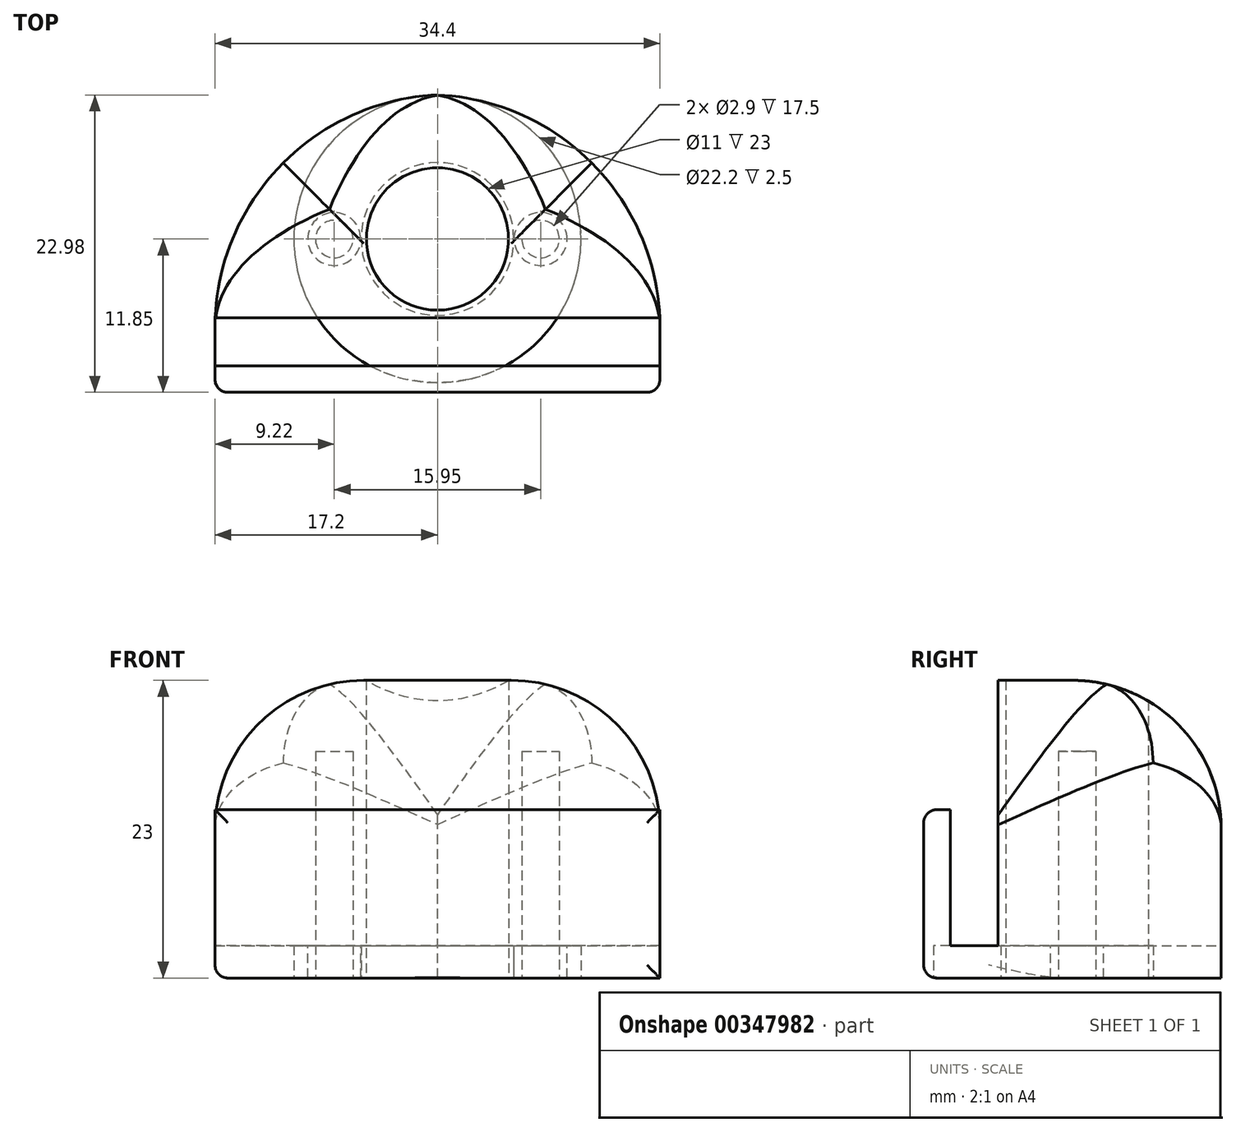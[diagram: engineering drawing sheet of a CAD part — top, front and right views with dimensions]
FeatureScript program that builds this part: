
annotation { "Feature Type Name" : "Feature", "Feature Type Description" : "" }
export const myFeature = defineFeature(function(context is Context, id is Id, definition is map)
    precondition{}
    {
        {
            var Q0;
            Q0=qCreatedBy(makeId("Top.planeOp"),FACE);
            var sketch = newSketch(context, id + "F0", { "sketchPlane" : qUnion([Q0])});
            skCircle(sketch, "E0", {"center": v(0, 0) * mm, "radius": 5.5 * mm});
            skLineSegment(sketch, "E1.bottom", {"start": v(17.2, 11.15) * mm, "end": v(-17.2, 11.15) * mm});
            skLineSegment(sketch, "E1.top", {"start": v(17.2, -11.85) * mm, "end": v(-17.2, -11.85) * mm});
            skLineSegment(sketch, "E1.left", {"start": v(17.2, 11.15) * mm, "end": v(17.2, -11.85) * mm});
            skLineSegment(sketch, "E1.right", {"start": v(-17.2, 11.15) * mm, "end": v(-17.2, -11.85) * mm});
            skPoint(sketch, "E1.middle", {"position": v(0, -0.35) * mm});
            skSolve(sketch);
        }
        {
            var Q0;
            Q0=makeQuery(id+"F0.imprint","IMPRINT",FACE,{"disambiguationData":[TD([[makeQuery(id+"F0.imprint","IMPRINT",EDGE,{"derivedFrom":sQuery(id+"F0.wireOp",EDGE,"E0")}),-1.0]])]});
            extrude(context, id + "F1", {"entities" : qUnion([Q0]), "depth" : 23 * mm});
        }
        {
            var Q0;
            Q0=makeQuery(id+"F1.opExtrude","CAP_FACE",FACE,{"disambiguationData":[OSD([sQuery(id+"F0.wireOp",EDGE,"E0"),sQuery(id+"F0.wireOp",EDGE,"E1.bottom"),sQuery(id+"F0.wireOp",EDGE,"E1.top"),sQuery(id+"F0.wireOp",EDGE,"E1.left"),sQuery(id+"F0.wireOp",EDGE,"E1.right"),sQuery(id+"F0.wireOp",EDGE,"J5Xj3zVj-uTtx-Os8S-LOdU-LLNhaVreQnM7")])],"isStart":true});
            var sketch = newSketch(context, id + "F2", { "sketchPlane" : qUnion([Q0])});
            skCircle(sketch, "E2", {"center": v(0, 0) * mm, "radius": 11.1 * mm});
            skCircle(sketch, "E3", {"center": v(0, 0) * mm, "radius": 5.3 * mm});
            skCircle(sketch, "E4", {"center": v(0, 0) * mm, "radius": 5.9 * mm});
            skSolve(sketch);
        }
        {
            var Q0;
            Q0=makeQuery(id+"F2.imprint","IMPRINT",FACE,{"disambiguationData":[TD([[makeQuery(id+"F2.imprint","IMPRINT",EDGE,{"derivedFrom":sQuery(id+"F2.wireOp",EDGE,"E2")}),1.0]])]});
            extrude(context, id + "F3", {"entities" : qUnion([Q0]), "operationType" : NewBodyOperationType.REMOVE, "oppositeDirection" : true, "depth" : 2.5 * mm});
        }
        {
            var Q0;
            Q0=makeQuery(id+"F3.boolean.opBoolean","COPY",FACE,{"derivedFrom":makeQuery(id+"F3.opExtrude","CAP_FACE",FACE,{"disambiguationData":[OSD([sQuery(id+"F0.wireOp",EDGE,"E0"),sQuery(id+"F2.wireOp",EDGE,"E2")])],"isStart":false})});
            var sketch = newSketch(context, id + "F4", { "sketchPlane" : qUnion([Q0])});
            skCircle(sketch, "E5", {"center": v(-7.98, 0) * mm, "radius": 1.45 * mm});
            skCircle(sketch, "E6", {"center": v(7.97, 0) * mm, "radius": 1.45 * mm});
            skCircle(sketch, "E7", {"center": v(7.97, 0) * mm, "radius": 2.05 * mm});
            skCircle(sketch, "E8", {"center": v(-7.98, 0) * mm, "radius": 2.05 * mm});
            skSolve(sketch);
        }
        {
            var Q0;
            Q0=makeQuery(id+"F4.imprint","IMPRINT",FACE,{"disambiguationData":[TD([[makeQuery(id+"F4.imprint","IMPRINT",EDGE,{"derivedFrom":sQuery(id+"F4.wireOp",EDGE,"E6")}),1.0]])]});
            var Q1;
            Q1=makeQuery(id+"F4.imprint","IMPRINT",FACE,{"disambiguationData":[TD([[makeQuery(id+"F4.imprint","IMPRINT",EDGE,{"derivedFrom":sQuery(id+"F4.wireOp",EDGE,"E5")}),1.0]])]});
            extrude(context, id + "F5", {"entities" : qUnion([Q0, Q1]), "operationType" : NewBodyOperationType.REMOVE, "oppositeDirection" : true, "depth" : 15 * mm});
        }
        {
            var Q0;
            Q0=makeQuery(id+"F1.opExtrude","CAP_FACE",FACE,{"disambiguationData":[OSD([sQuery(id+"F0.wireOp",EDGE,"E0"),sQuery(id+"F0.wireOp",EDGE,"E1.bottom"),sQuery(id+"F0.wireOp",EDGE,"E1.top"),sQuery(id+"F0.wireOp",EDGE,"E1.left"),sQuery(id+"F0.wireOp",EDGE,"E1.right"),sQuery(id+"F0.wireOp",EDGE,"J5Xj3zVj-uTtx-Os8S-LOdU-LLNhaVreQnM7")])],"isStart":false});
            var sketch = newSketch(context, id + "F6", { "sketchPlane" : qUnion([Q0])});
            skLineSegment(sketch, "E9", {"start": v(-17.2, -6.1) * mm, "end": v(17.2, -6.1) * mm});
            skLineSegment(sketch, "E10", {"start": v(17.2, -6.1) * mm, "end": v(17.2, -9.8) * mm});
            skLineSegment(sketch, "E11", {"start": v(17.2, -9.8) * mm, "end": v(-17.2, -9.8) * mm});
            skSolve(sketch);
        }
        {
            var Q0;
            {var subQ0=sQuery(id+"F6.wireOp",EDGE,"E9");Q0=makeQuery(id+"F6.imprint","IMPRINT",FACE,{"disambiguationData":[TD([[makeQuery(id+"F6.imprint","IMPRINT",EDGE,{"derivedFrom":subQ0}),-1.0]])]});}
            extrude(context, id + "F7", {"entities" : qUnion([Q0]), "operationType" : NewBodyOperationType.REMOVE, "oppositeDirection" : true, "depth" : 20.5 * mm});
        }
        {
            var Q0;
            {var subQ0=sQuery(id+"F6.wireOp",EDGE,"E11");Q0=makeQuery(id+"F6.imprint","IMPRINT",FACE,{"disambiguationData":[TD([[makeQuery(id+"F6.imprint","IMPRINT",EDGE,{"derivedFrom":subQ0}),1.0]])]});}
            extrude(context, id + "F8", {"entities" : qUnion([Q0]), "operationType" : NewBodyOperationType.REMOVE, "oppositeDirection" : true, "depth" : 10 * mm});
        }
        {
            var Q0;
            {var subQ0=sQuery(id+"F0.wireOp",EDGE,"E1.right");var subQ1=sQuery(id+"F0.wireOp",EDGE,"E1.bottom");Q0=makeQuery(id+"F7.boolean.opBoolean","SPLIT",EDGE,{"disambiguationData":[TD([makeQuery(id+"F1.opExtrude","SWEPT_FACE",FACE,{"disambiguationData":[OSD([subQ1])]})])],"derivedFrom":makeQuery(id+"F1.opExtrude","CAP_EDGE",EDGE,{"disambiguationData":[OSD([subQ0])],"isStart":false})});}
            var Q1;
            Q1=makeQuery(id+"F1.opExtrude","CAP_EDGE",EDGE,{"disambiguationData":[OSD([sQuery(id+"F0.wireOp",EDGE,"E1.bottom")])],"isStart":false});
            var Q2;
            {var subQ0=sQuery(id+"F0.wireOp",EDGE,"E1.left");var subQ1=sQuery(id+"F0.wireOp",EDGE,"E1.bottom");Q2=makeQuery(id+"F7.boolean.opBoolean","SPLIT",EDGE,{"disambiguationData":[TD([makeQuery(id+"F1.opExtrude","SWEPT_FACE",FACE,{"disambiguationData":[OSD([subQ1])]})])],"derivedFrom":makeQuery(id+"F1.opExtrude","CAP_EDGE",EDGE,{"disambiguationData":[OSD([subQ0])],"isStart":false})});}
            var Q3;
            Q3=makeQuery(id+"F8.boolean.opBoolean","COPY",EDGE,{"derivedFrom":makeQuery(id+"F8.opExtrude","CAP_EDGE",EDGE,{"disambiguationData":[OSD([sQuery(id+"F0.wireOp",EDGE,"E1.right")])],"isStart":false})});
            var Q4;
            Q4=makeQuery(id+"F8.boolean.opBoolean","COPY",EDGE,{"derivedFrom":makeQuery(id+"F8.opExtrude","CAP_EDGE",EDGE,{"disambiguationData":[OSD([sQuery(id+"F0.wireOp",EDGE,"E1.left")])],"isStart":false})});
            fillet(context, id + "F9", {"entities" : qUnion([Q0, Q1, Q2, Q3, Q4]), "radius" : 11.5 * mm, "tangentPropagation" : true, "allowEdgeOverflow" : false});
        }
        {
            var Q0;
            Q0=makeQuery(id+"F7.boolean.opBoolean","COPY",EDGE,{"derivedFrom":makeQuery(id+"F7.opExtrude","CAP_EDGE",EDGE,{"disambiguationData":[OSD([sQuery(id+"F6.wireOp",EDGE,"E9")])],"isStart":true})});
            var Q1;
            Q1=makeQuery(id+"F8.boolean.opBoolean","COPY",EDGE,{"derivedFrom":makeQuery(id+"F8.opExtrude","CAP_EDGE",EDGE,{"disambiguationData":[OSD([sQuery(id+"F6.wireOp",EDGE,"E11")])],"isStart":false})});
            var Q2;
            Q2=makeQuery(id+"F1.opExtrude","SWEPT_FACE",FACE,{"disambiguationData":[OSD([sQuery(id+"F0.wireOp",EDGE,"E1.top")])]});
            var Q3;
            Q3=makeQuery(id+"F1.opExtrude","CAP_EDGE",EDGE,{"disambiguationData":[OSD([sQuery(id+"F0.wireOp",EDGE,"E1.right")])],"isStart":true});
            fillet(context, id + "F10", {"entities" : qUnion([Q0, Q1, Q2, Q3]), "radius" : 1 * mm, "tangentPropagation" : true, "allowEdgeOverflow" : false});
        }
        {
            var Q0;
            Q0=makeQuery(id+"F1.opExtrude","SWEPT_EDGE",EDGE,{"disambiguationData":[OSD([sQuery(id+"F0.wireOp",EDGE,"E1.bottom"),sQuery(id+"F0.wireOp",EDGE,"E1.left")])]});
            var Q1;
            Q1=makeQuery(id+"F1.opExtrude","SWEPT_EDGE",EDGE,{"disambiguationData":[OSD([sQuery(id+"F0.wireOp",EDGE,"E1.bottom"),sQuery(id+"F0.wireOp",EDGE,"E1.right")])]});
            fillet(context, id + "F11", {"entities" : qUnion([Q0, Q1]), "radius" : 18 * mm, "allowEdgeOverflow" : false});
        }
        {
            var Q0;
            {var subQ0=sQuery(id+"F0.wireOp",EDGE,"E1.bottom");Q0=makeQuery(id+"F11.opFillet","BLEND_EDGE",EDGE,{"blendedFrom":[makeQuery(id+"F1.opExtrude","SWEPT_EDGE",EDGE,{"disambiguationData":[OSD([subQ0,sQuery(id+"F0.wireOp",EDGE,"E1.right")])]}),makeQuery(id+"F9.opFillet","BLEND_FACE",FACE,{"disambiguationData":[OSD([subQ0])]})],"blendedInto":[makeQuery(id+"F9.opFillet","BLEND_FACE",FACE,{"disambiguationData":[OSD([subQ0])]})]});}
            var Q1;
            {var subQ0=sQuery(id+"F0.wireOp",EDGE,"E1.right");var subQ1=sQuery(id+"F0.wireOp",EDGE,"E1.bottom");Q1=makeQuery(id+"F11.opFillet","BLEND_EDGE",EDGE,{"blendedFrom":[makeQuery(id+"F1.opExtrude","SWEPT_EDGE",EDGE,{"disambiguationData":[OSD([subQ1,subQ0])]}),makeQuery(id+"F9.opFillet","BLEND_FACE",FACE,{"disambiguationData":[OSD([subQ0]),TDD([makeQuery(id+"F7.boolean.opBoolean","SPLIT",EDGE,{"disambiguationData":[TD([makeQuery(id+"F1.opExtrude","SWEPT_FACE",FACE,{"disambiguationData":[OSD([subQ1])]})])],"derivedFrom":makeQuery(id+"F1.opExtrude","CAP_EDGE",EDGE,{"disambiguationData":[OSD([subQ0])],"isStart":false})})])]})],"blendedInto":[makeQuery(id+"F9.opFillet","BLEND_FACE",FACE,{"disambiguationData":[OSD([subQ0]),TDD([makeQuery(id+"F7.boolean.opBoolean","SPLIT",EDGE,{"disambiguationData":[TD([makeQuery(id+"F1.opExtrude","SWEPT_FACE",FACE,{"disambiguationData":[OSD([subQ1])]})])],"derivedFrom":makeQuery(id+"F1.opExtrude","CAP_EDGE",EDGE,{"disambiguationData":[OSD([subQ0])],"isStart":false})})])]})]});}
            var Q2;
            {var subQ0=sQuery(id+"F0.wireOp",EDGE,"E1.left");var subQ1=sQuery(id+"F0.wireOp",EDGE,"E1.bottom");Q2=makeQuery(id+"F11.opFillet","BLEND_EDGE",EDGE,{"blendedFrom":[makeQuery(id+"F1.opExtrude","SWEPT_EDGE",EDGE,{"disambiguationData":[OSD([subQ1,subQ0])]}),makeQuery(id+"F9.opFillet","BLEND_FACE",FACE,{"disambiguationData":[OSD([subQ0]),TDD([makeQuery(id+"F7.boolean.opBoolean","SPLIT",EDGE,{"disambiguationData":[TD([makeQuery(id+"F1.opExtrude","SWEPT_FACE",FACE,{"disambiguationData":[OSD([subQ1])]})])],"derivedFrom":makeQuery(id+"F1.opExtrude","CAP_EDGE",EDGE,{"disambiguationData":[OSD([subQ0])],"isStart":false})})])]})],"blendedInto":[makeQuery(id+"F9.opFillet","BLEND_FACE",FACE,{"disambiguationData":[OSD([subQ0]),TDD([makeQuery(id+"F7.boolean.opBoolean","SPLIT",EDGE,{"disambiguationData":[TD([makeQuery(id+"F1.opExtrude","SWEPT_FACE",FACE,{"disambiguationData":[OSD([subQ1])]})])],"derivedFrom":makeQuery(id+"F1.opExtrude","CAP_EDGE",EDGE,{"disambiguationData":[OSD([subQ0])],"isStart":false})})])]})]});}
            var Q3;
            {var subQ0=sQuery(id+"F0.wireOp",EDGE,"E1.bottom");Q3=makeQuery(id+"F11.opFillet","BLEND_EDGE",EDGE,{"blendedFrom":[makeQuery(id+"F1.opExtrude","SWEPT_EDGE",EDGE,{"disambiguationData":[OSD([subQ0,sQuery(id+"F0.wireOp",EDGE,"E1.left")])]}),makeQuery(id+"F9.opFillet","BLEND_FACE",FACE,{"disambiguationData":[OSD([subQ0])]})],"blendedInto":[makeQuery(id+"F9.opFillet","BLEND_FACE",FACE,{"disambiguationData":[OSD([subQ0])]})]});}
            fillet(context, id + "F12", {"entities" : qUnion([Q0, Q1, Q2, Q3]), "radius" : 6 * mm, "allowEdgeOverflow" : false});
        }
        {
            var Q0;
            Q0=makeQuery(id+"F4.imprint","IMPRINT",FACE,{"disambiguationData":[TD([[makeQuery(id+"F4.imprint","IMPRINT",EDGE,{"derivedFrom":sQuery(id+"F4.wireOp",EDGE,"E6")}),-1.0]])]});
            var Q1;
            Q1=makeQuery(id+"F4.imprint","IMPRINT",FACE,{"disambiguationData":[TD([[makeQuery(id+"F4.imprint","IMPRINT",EDGE,{"derivedFrom":sQuery(id+"F4.wireOp",EDGE,"E5")}),-1.0]])]});
            extrude(context, id + "F13", {"entities" : qUnion([Q0, Q1]), "operationType" : NewBodyOperationType.ADD, "depth" : 2.5 * mm});
        }
    });
